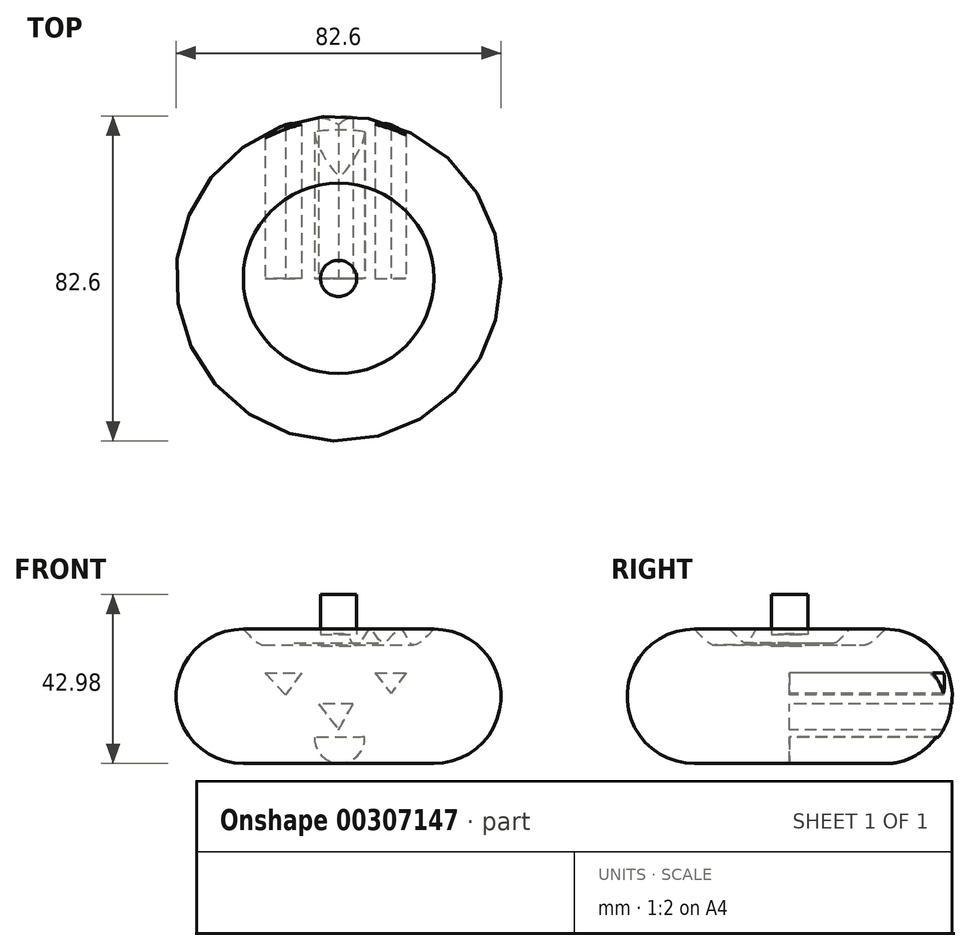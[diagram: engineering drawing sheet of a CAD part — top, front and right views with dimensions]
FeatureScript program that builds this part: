
annotation { "Feature Type Name" : "Feature", "Feature Type Description" : "" }
export const myFeature = defineFeature(function(context is Context, id is Id, definition is map)
    precondition{}
    {
        {
            var Q0;
            Q0=qCreatedBy(makeId("Front.planeOp"),FACE);
            var sketch = newSketch(context, id + "F0", { "sketchPlane" : qUnion([Q0])});
            skLineSegment(sketch, "E0", {"start": v(0, 88.75) * mm, "end": v(0, -90.28) * mm});
            skSolve(sketch);
        }
        {
            var Q0;
            Q0=qCreatedBy(makeId("Front.planeOp"),FACE);
            var sketch = newSketch(context, id + "F1", { "sketchPlane" : qUnion([Q0])});
            skLineSegment(sketch, "E1", {"start": v(0, 0) * mm, "end": v(24.2, 0) * mm});
            skArc(sketch, "E2", {"start": v(24.2, 0) * mm, "mid": v(41.3, 17.1) * mm, "end": v(24.2, 34.2) * mm});
            skFitSpline(sketch, "E3", {"points": [v(24.2, 34.2) * mm, v(18.44, 30.35) * mm, v(15.75, 34.2) * mm, v(11.14, 30.74) * mm, v(8.07, 34.2) * mm, v(4.6, 29.97) * mm, v(2.08, 32.66) * mm, v(0, 32.66) * mm], "startDerivative": vector(-38.03, -41.07) * mm, "endDerivative": vector(-22.36, -8.63) * mm});
            skFitSpline(sketch, "E4", {"points": [v(0, 32.66) * mm, v(0, -1.07) * mm], "startDerivative": vector(0, -33.73) * mm, "endDerivative": vector(0, -33.73) * mm});
            skSolve(sketch);
        }
        {
            var Q0;
            {var subQ0=sQuery(id+"F1.wireOp",EDGE,"E1");Q0=makeQuery(id+"F1.imprint","IMPRINT",FACE,{"disambiguationData":[TD([[makeQuery(id+"F1.imprint","IMPRINT",EDGE,{"derivedFrom":subQ0}),1.0]])]});}
            var Q1;
            Q1=sQuery(id+"F0.wireOp",EDGE,"E0");
            revolve(context, id + "F2", {"entities" : qUnion([Q0]), "axis" : qUnion([Q1]), "revolveType" : RevolveType.FULL});
        }
        {
            var Q0;
            Q0=qCreatedBy(makeId("Front.planeOp"),FACE);
            var sketch = newSketch(context, id + "F3", { "sketchPlane" : qUnion([Q0])});
            skLineSegment(sketch, "E5", {"start": v(0, 42.98) * mm, "end": v(4.6, 42.98) * mm});
            skLineSegment(sketch, "E6", {"start": v(4.6, 42.98) * mm, "end": v(4.6, 32.84) * mm});
            skLineSegment(sketch, "E7", {"start": v(4.6, 32.84) * mm, "end": v(0, 32.84) * mm});
            skLineSegment(sketch, "E8", {"start": v(0, 32.84) * mm, "end": v(0, 42.98) * mm});
            skSolve(sketch);
        }
        {
            var Q0;
            Q0 = qSketchRegion(id + "F3", true);
            var Q1;
            Q1=sQuery(id+"F3.wireOp",EDGE,"E8");
            revolve(context, id + "F4", {"entities" : qUnion([Q0]), "axis" : qUnion([Q1]), "revolveType" : RevolveType.FULL});
        }
        {
            var Q0;
            Q0=qCreatedBy(makeId("Front.planeOp"),FACE);
            var sketch = newSketch(context, id + "F5", { "sketchPlane" : qUnion([Q0])});
            skLineSegment(sketch, "E9", {"start": v(-18.66, 23.06) * mm, "end": v(-9.45, 23.06) * mm});
            skLineSegment(sketch, "E10", {"start": v(-9.45, 23.06) * mm, "end": v(-13.48, 17.44) * mm});
            skLineSegment(sketch, "E11", {"start": v(-13.48, 17.44) * mm, "end": v(-18.66, 23.06) * mm});
            skLineSegment(sketch, "E12", {"start": v(17.18, 23.06) * mm, "end": v(13.29, 17.88) * mm});
            skLineSegment(sketch, "E13", {"start": v(9.26, 23.02) * mm, "end": v(17.18, 23.06) * mm});
            skLineSegment(sketch, "E14", {"start": v(9.26, 23.02) * mm, "end": v(13.29, 17.88) * mm});
            skSolve(sketch);
        }
        {
            var Q0;
            Q0 = qSketchRegion(id + "F5", true);
            extrude(context, id + "F6", {"entities" : qUnion([Q0]), "operationType" : NewBodyOperationType.REMOVE, "oppositeDirection" : true, "depth" : 50.8 * mm});
        }
        {
            var Q0;
            Q0=qCreatedBy(makeId("Front.planeOp"),FACE);
            var sketch = newSketch(context, id + "F7", { "sketchPlane" : qUnion([Q0])});
            skLineSegment(sketch, "E15", {"start": v(3.65, 15.15) * mm, "end": v(-5.05, 15.15) * mm});
            skLineSegment(sketch, "E16", {"start": v(-5.05, 15.15) * mm, "end": v(0, 8.62) * mm});
            skLineSegment(sketch, "E17", {"start": v(0, 8.62) * mm, "end": v(3.65, 15.15) * mm});
            skSolve(sketch);
        }
        {
            var Q0;
            Q0 = qSketchRegion(id + "F7", true);
            extrude(context, id + "F8", {"entities" : qUnion([Q0]), "operationType" : NewBodyOperationType.REMOVE, "oppositeDirection" : true, "depth" : 50.8 * mm});
        }
        {
            var Q0;
            Q0=qCreatedBy(makeId("Front.planeOp"),FACE);
            var sketch = newSketch(context, id + "F9", { "sketchPlane" : qUnion([Q0])});
            skArc(sketch, "E18", {"start": v(-6.11, 6.6) * mm, "mid": v(0.34, 0.12) * mm, "end": v(6.66, 6.74) * mm});
            skLineSegment(sketch, "E19", {"start": v(6.66, 6.74) * mm, "end": v(-6.11, 6.6) * mm});
            skSolve(sketch);
        }
        {
            var Q0;
            Q0 = qSketchRegion(id + "F9", true);
            extrude(context, id + "F10", {"entities" : qUnion([Q0]), "operationType" : NewBodyOperationType.REMOVE, "oppositeDirection" : true, "depth" : 50.8 * mm});
        }
    });
